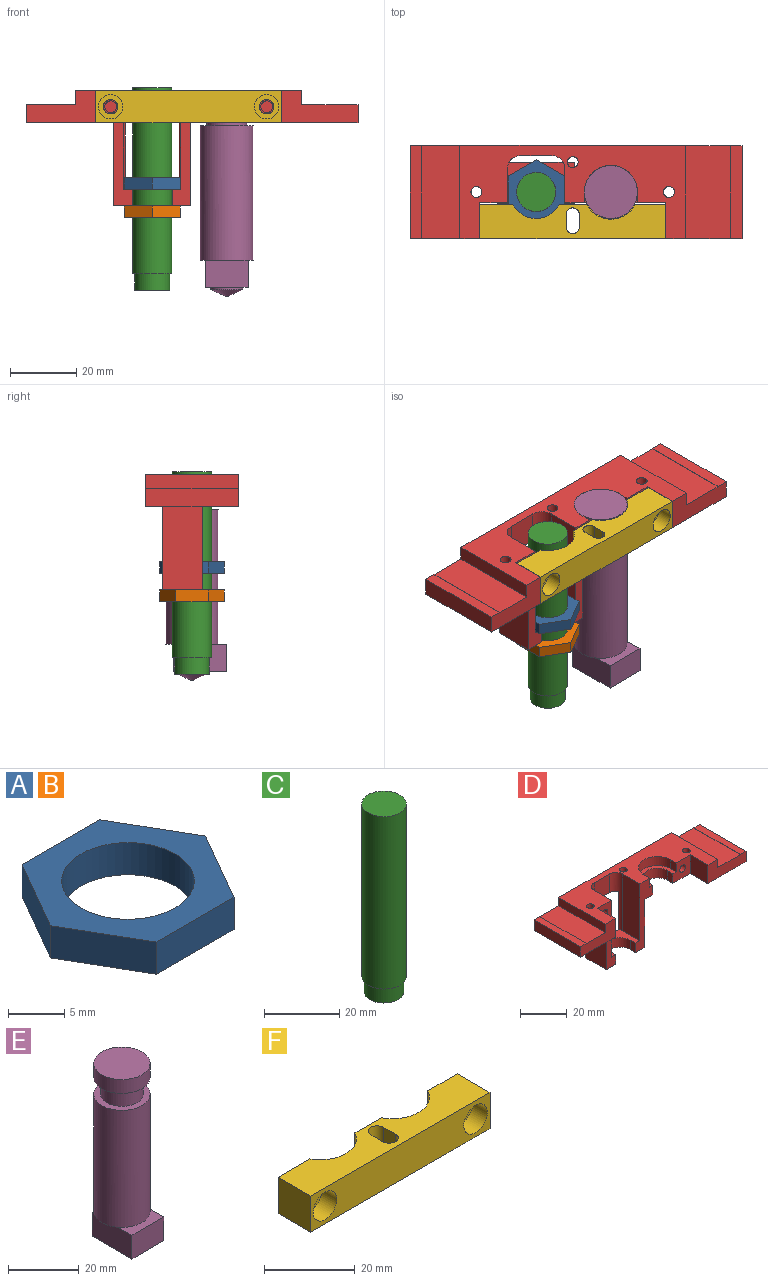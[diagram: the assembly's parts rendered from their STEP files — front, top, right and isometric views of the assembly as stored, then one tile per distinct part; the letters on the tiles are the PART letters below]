
ASSEMBLY  parts=6 mates=11
PART A: 9 faces, bbox 19.5x16.9x3.5 mm
  f0: plane 9.76x3.5mm, normal (0,-1,0), area 34.2mm2, adj f1,f6,f7,f8
  f1: plane 8.45x4.88mm, normal (0.87,-0.5,0), area 34.2mm2, adj f0,f2,f7,f8
  f2: plane 8.45x4.88mm, normal (0.87,0.5,0), area 34.2mm2, adj f1,f3,f7,f8
  f3: plane 9.76x3.5mm, normal (0,1,0), area 34.2mm2, adj f2,f4,f7,f8
  f4: plane 8.45x4.88mm, normal (-0.87,0.5,0), area 34.2mm2, adj f3,f6,f7,f8
  f5: cylinder r=5.9mm len=11.8mm, axis (0,0,-1), area 129.7mm2, adj f7,f8
  f6: plane 8.45x4.88mm, normal (-0.87,-0.5,0), area 34.2mm2, adj f0,f4,f7,f8
  f7: plane 19.51x16.9mm, normal (0,0,1), area 138mm2, adj f0,f1,f2,f3,f4,f5,f6
  f8: plane 19.51x16.9mm, normal (0,0,-1), area 138mm2, adj f0,f1,f2,f3,f4,f5,f6
PART B: same geometry as A
PART C: 5 faces, bbox 11.8x11.8x61 mm
  f0: plane 10.5x10.5mm, normal (0,0,-1), area 86.6mm2, adj f1
  f1: cylinder r=5.25mm len=10.5mm, axis (0,0,-1), area 164.9mm2, adj f0,f2
  f2: plane 11.8x11.8mm, normal (0,0,-1), area 22.8mm2, adj f1,f3
  f3: cylinder r=5.9mm len=56mm, axis (0,0,-1), area 2076mm2, adj f2,f4
  f4: plane 11.8x11.8mm, normal (0,0,1), area 109.4mm2, adj f3
PART D: 48 faces, bbox 100x28x34.8 mm
  f0: plane 68x28mm, normal (0,0,1), area 885.5mm2, adj f1,f5,f6,f9,f11,f16,f17,f22
  f1: cylinder r=8mm len=16mm, axis (0,0,1), area 118.1mm2, adj f0,f8,f46,f47
  f2: plane 100x28mm, normal (0,0,-1), area 1767.3mm2, adj f5,f6,f7,f9,f11,f12,f21,f22
  f3: plane 23.3x12.3mm, normal (0,0,-1), area 190.4mm2, adj f5,f10,f24,f31,f32,f33,f36,f37
  f4: plane 17.3x12.3mm, normal (0,0,1), area 115.9mm2, adj f5,f10,f24,f26,f28,f29,f30,f31
  f5: plane 34.75x10.5mm, normal (0,-1,0), area 155.4mm2, adj f0,f2,f3,f4,f8,f29,f33,f35
  f6: plane 10.5x9.75mm, normal (0,-1,0), area 83mm2, adj f0,f2,f8,f25,f34,f40,f47
  f7: cylinder r=6mm len=12mm, axis (0,0,-1), area 95.2mm2, adj f2,f8,f34,f35
  f8: plane 16x11.3mm, normal (0,0,1), area 57.2mm2, adj f1,f5,f6,f7,f34,f35,f46,f47
  f9: plane 100x9.75mm, normal (0,1,0), area 836.5mm2, adj f0,f2,f12,f13,f14,f15,f16,f17
  f10: cylinder r=6mm len=12mm, axis (0,0,-1), area 94.2mm2, adj f3,f4,f36,f37
  f11: plane 23x9.75mm, normal (0,-1,0), area 150.6mm2, adj f0,f2,f12,f13,f14,f15,f16,f25
  f12: plane 28x5.5mm, normal (1,0,0), area 154mm2, adj f2,f9,f11,f13
  f13: plane 28x3.5mm, normal (0,0,1), area 98mm2, adj f9,f11,f12,f14
  f14: plane 28x0.1mm, normal (-1,0,0), area 2.8mm2, adj f9,f11,f13,f15
  f15: plane 28x13.5mm, normal (0,0,1), area 378mm2, adj f9,f11,f14,f16
  f16: plane 28x4.35mm, normal (1,0,0), area 121.8mm2, adj f0,f9,f11,f15
  f17: plane 28x4.35mm, normal (-1,0,0), area 121.8mm2, adj f0,f9,f18,f22
  f18: plane 28x11.5mm, normal (0,0,1), area 322mm2, adj f9,f17,f19,f22
  f19: plane 28x0.1mm, normal (1,0,0), area 2.8mm2, adj f9,f18,f20,f22
  f20: plane 28x3.5mm, normal (0,0,1), area 98mm2, adj f9,f19,f21,f22
  f21: plane 28x5.5mm, normal (-1,0,0), area 154mm2, adj f2,f9,f20,f22
  f22: plane 21x9.75mm, normal (0,-1,0), area 139.8mm2, adj f0,f2,f17,f18,f19,f20,f21,f23
  f23: plane 10.7x9.75mm, normal (1,0,0), area 104.3mm2, adj f0,f2,f22,f24
  f24: plane 34.75x11mm, normal (0,-1,0), area 159.6mm2, adj f0,f2,f3,f4,f23,f30,f32,f36
  f25: plane 10.7x9.75mm, normal (-1,0,0), area 104.3mm2, adj f0,f2,f6,f11
  f26: cylinder r=4mm len=29.75mm, axis (0,0,1), area 103.4mm2, adj f0,f2,f4,f27,f30,f31
  f27: plane 9.75x9.3mm, normal (0,-1,0), area 90.7mm2, adj f0,f2,f26,f28
  f28: cylinder r=4mm len=29.75mm, axis (0,0,1), area 103.4mm2, adj f0,f2,f4,f27,f29,f31
  f29: plane 29.75x10.29mm, normal (-1,0,0), area 306.1mm2, adj f0,f4,f5,f28
  f30: plane 29.75x10.29mm, normal (1,0,0), area 306.1mm2, adj f0,f4,f24,f26
  f31: plane 25x23.3mm, normal (0,1,0), area 258.2mm2, adj f2,f3,f4,f26,f28,f32,f33,f42
  f32: plane 25x12.3mm, normal (-1,0,0), area 307.5mm2, adj f2,f3,f24,f31
  f33: plane 25x12.3mm, normal (1,0,0), area 307.5mm2, adj f2,f3,f5,f31,f42
  f34: plane 5.05x3.3mm, normal (-1,0,0), area 16.7mm2, adj f2,f6,f7,f8
  f35: plane 5.05x3.3mm, normal (1,0,0), area 16.7mm2, adj f2,f5,f7,f8
  f36: plane 5x3.3mm, normal (1,0,0), area 16.5mm2, adj f3,f4,f10,f24
  f37: plane 5x3.3mm, normal (-1,0,0), area 16.5mm2, adj f3,f4,f5,f10
  f38: cylinder r=1.79mm len=12mm, axis (0,-1,0), area 134.7mm2, adj f24,f39
  f39: plane 3.57x3.57mm, normal (0,-1,0), area 10mm2, adj f38
  f40: cylinder r=1.79mm len=12mm, axis (0,-1,0), area 134.7mm2, adj f6,f41
  f41: plane 3.57x3.57mm, normal (0,-1,0), area 10mm2, adj f40
  f42: plane 2.3x1.65mm, normal (0,0,1), area 3.2mm2, adj f31,f33,f43
  f43: cylinder r=1.65mm len=9.75mm, axis (0,0,1), area 101.1mm2, adj f0,f2,f42
  f44: cylinder r=1.65mm len=9.75mm, axis (0,0,1), area 101.1mm2, adj f0,f2
  f45: cylinder r=1.65mm len=9.75mm, axis (0,0,1), area 101.1mm2, adj f0,f2
  f46: plane 4.7x3.3mm, normal (1,0,0), area 15.5mm2, adj f0,f1,f5,f8
  f47: plane 4.7x3.3mm, normal (-1,0,0), area 15.5mm2, adj f0,f1,f6,f8
PART E: 20 faces, bbox 16x18.4x62.1 mm
  f0: plane 11.55x2.48mm, normal (0,0,-1), area 19.7mm2, adj f4,f14
  f1: plane 9.58x1.6mm, normal (0,0,-1), area 10.4mm2, adj f4,f13
  f2: plane 15.95x15.95mm, normal (0,0,1), area 199.8mm2, adj f8
  f3: plane 9.58x1.6mm, normal (0,0,-1), area 10.4mm2, adj f4,f15
  f4: cylinder r=7.97mm len=40.5mm, axis (0,0,-1), area 2029.4mm2, adj f0,f1,f3,f5,f9,f10,f11
  f5: plane 15.95x15.95mm, normal (0,0,1), area 86.7mm2, adj f4,f6
  f6: cylinder r=6mm len=12mm, axis (0,0,-1), area 220.5mm2, adj f5,f7
  f7: plane 15.95x15.95mm, normal (0,0,-1), area 86.7mm2, adj f6,f8
  f8: cylinder r=7.97mm len=15.95mm, axis (0,0,-1), area 240.5mm2, adj f2,f7
  f9: plane 0.71x0.6mm, normal (0,0,1), area 0.2mm2, adj f4,f13,f14
  f10: plane 0.71x0.6mm, normal (0,0,1), area 0.2mm2, adj f4,f14,f15
  f11: plane 12.75x5.6mm, normal (0,0,1), area 43mm2, adj f4,f12,f13,f15
  f12: plane 12.75x8.2mm, normal (0,-1,0), area 104.5mm2, adj f11,f13,f15,f16
  f13: plane 15.89x8.2mm, normal (-1,0,0), area 130.3mm2, adj f1,f9,f11,f12,f14,f16
  f14: plane 12.75x8.2mm, normal (0,1,0), area 104.5mm2, adj f0,f9,f10,f13,f15,f16
  f15: plane 15.89x8.2mm, normal (1,0,0), area 130.3mm2, adj f3,f10,f11,f12,f14,f16
  f16: plane 15.89x12.75mm, normal (0,0,-1), area 128.7mm2, adj f12,f13,f14,f15,f17
  f17: cylinder r=4.85mm len=9.7mm, axis (0,0,1), area 21.3mm2, adj f16,f19
  f18: plane 0.7x0.7mm, normal (0,0,-1), area 0.4mm2, adj f19
  f19: cone r=0.35mm half-angle=66deg, axis (0,0,1), area 80.4mm2, adj f17,f18
PART F: 22 faces, bbox 56x10.2x9.8 mm
  f0: cylinder r=6mm len=9.29mm, axis (0,0,1), area 51.5mm2, adj f1,f2,f6,f20
  f1: plane 10.82x9.75mm, normal (0,1,0), area 92.6mm2, adj f0,f6,f7,f18,f20,f21
  f2: plane 11.86x9.75mm, normal (0,1,0), area 87.8mm2, adj f0,f4,f6,f7,f9,f20,f21
  f3: plane 10.2x9.75mm, normal (-1,0,0), area 99.5mm2, adj f6,f7,f8,f19
  f4: cylinder r=2.18mm len=5.53mm, axis (0,1,0), area 75.9mm2, adj f2,f12
  f5: cylinder r=2.18mm len=5.53mm, axis (0,1,0), area 75.9mm2, adj f10,f19
  f6: plane 56x10.2mm, normal (0,0,-1), area 487.5mm2, adj f0,f1,f2,f3,f8,f9,f14,f15
  f7: plane 56x10.2mm, normal (0,0,1), area 456.1mm2, adj f1,f2,f3,f8,f9,f14,f15,f16
  f8: plane 56x9.75mm, normal (0,-1,0), area 461mm2, adj f3,f6,f7,f9,f11,f13
  f9: plane 10.2x9.75mm, normal (1,0,0), area 99.5mm2, adj f2,f6,f7,f8
  f10: plane 7.36x7.36mm, normal (0,-1,0), area 27.6mm2, adj f5,f11
  f11: cylinder r=3.68mm len=7.36mm, axis (0,-1,0), area 107.8mm2, adj f8,f10
  f12: plane 7.36x7.36mm, normal (0,-1,0), area 27.6mm2, adj f4,f13
  f13: cylinder r=3.68mm len=7.36mm, axis (0,-1,0), area 107.8mm2, adj f8,f12
  f14: cylinder r=2mm len=9.75mm, axis (0,0,1), area 61.3mm2, adj f6,f7,f15,f17
  f15: plane 9.75x3.7mm, normal (1,0,0), area 36.1mm2, adj f6,f7,f14,f16
  f16: cylinder r=2mm len=9.75mm, axis (0,0,1), area 61.3mm2, adj f6,f7,f15,f17
  f17: plane 9.75x3.7mm, normal (-1,0,0), area 36.1mm2, adj f6,f7,f14,f16
  f18: cylinder r=8mm len=14.08mm, axis (0,0,1), area 167.8mm2, adj f1,f6,f7,f19
  f19: plane 9.96x9.75mm, normal (0,1,0), area 82.1mm2, adj f3,f5,f6,f7,f18
  f20: plane 14.53x4.4mm, normal (0,0,1), area 31.4mm2, adj f0,f1,f2,f21
  f21: cylinder r=8.2mm len=14.53mm, axis (0,0,1), area 87.5mm2, adj f1,f2,f7,f20
PLACE A rot(axis=(0,0,1),30deg) t=(-71.39,-36.11,-8.36)mm
PLACE B rot(axis=(0,0,1),30deg) t=(-71.39,-36.11,-16.86)mm
PLACE C rot(axis=(0,0,1),83.1deg) t=(-71.39,-36.11,-38.77)mm
PLACE D t=(-9.39,-22.11,11.64)mm fixed
PLACE E t=(-48.89,-36.11,-29.66)mm
PLACE F t=(-9.39,-22.11,11.64)mm
MATE parallel A.f1 <-> D.f29  axis (1,0,0) through (-62.94,-36.11,-6.61)mm
MATE planar F.f3 <-> D.f23  axis (-1,0,0) through (-88.39,-45.01,16.52)mm
MATE planar D.f3 <-> B.f7  axis (0,0,-1) through (-71.39,-32.24,-13.36)mm
MATE parallel A.f6 <-> B.f6  axis (-0.5,-0.87,0) through (-75.61,-43.43,-6.61)mm
MATE planar D.f22 <-> F.f8  axis (0,-1,0) through (-94.39,-50.11,17.04)mm
MATE cylindrical C.f1 <-> D.f10  axis (0,0,-1) through (-71.39,-36.11,-33.77)mm
MATE cylindrical D.f38 <-> F.f5  axis (0,-1,0) through (-83.89,-33.41,16.52)mm
MATE fastened E.f4 <-> D.f1  axis (0,0,-1) through (-48.89,-36.11,16.69)mm
MATE cylindrical B.f5 <-> C.f1  axis (0,0,-1) through (-71.39,-36.11,-13.36)mm
MATE planar A.f8 <-> D.f4  axis (0,0,-1) through (-62.94,-31.24,-8.36)mm
MATE cylindrical A.f5 <-> C.f1  axis (0,0,1) through (-71.39,-36.11,-4.86)mm
